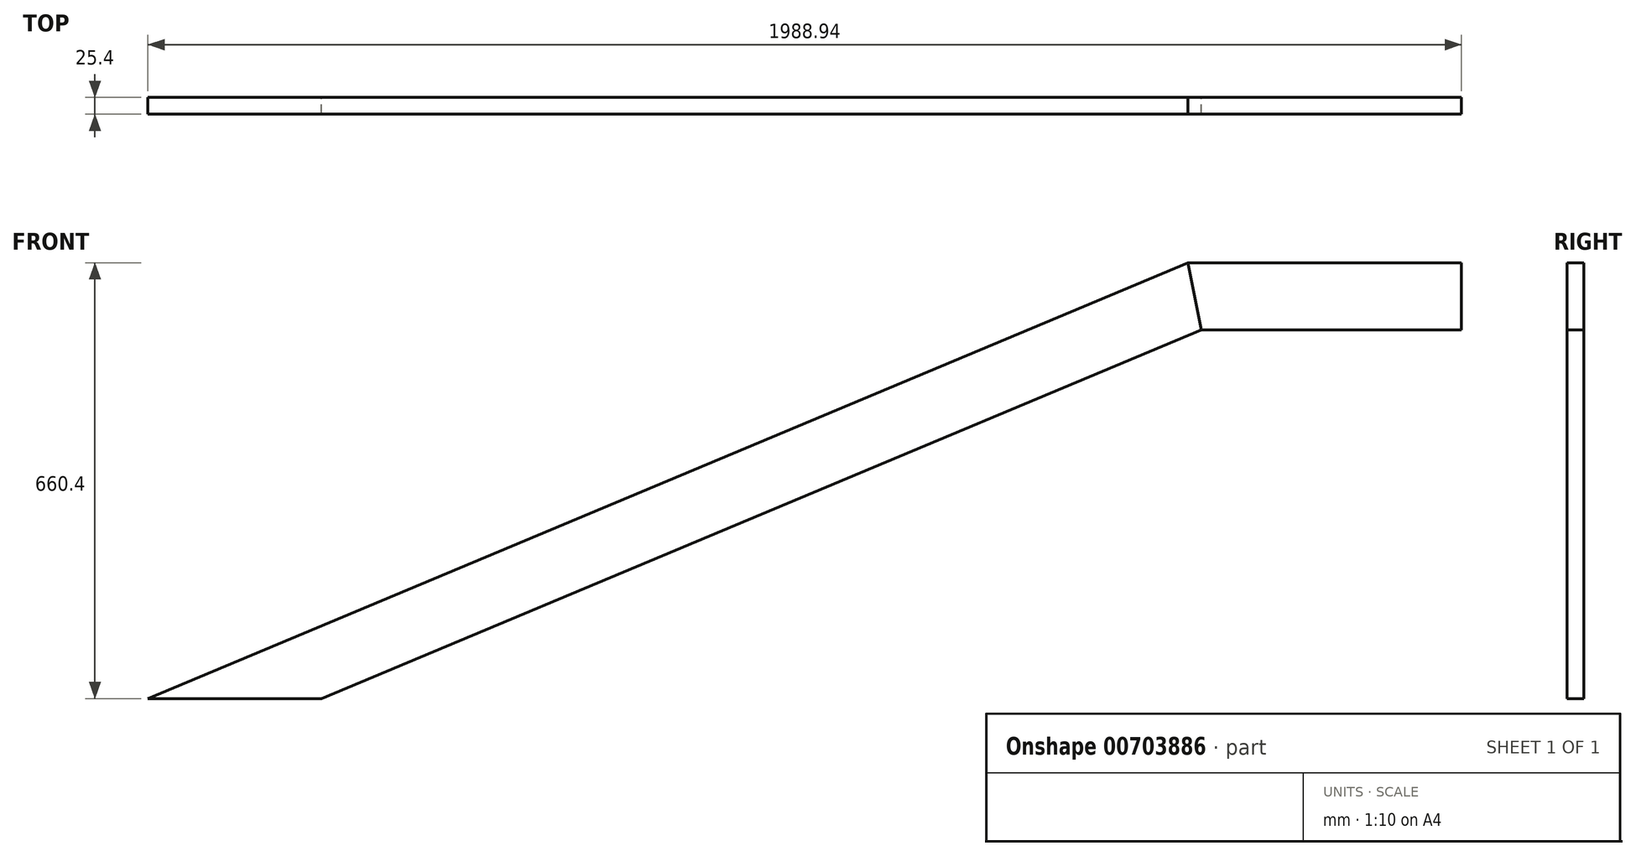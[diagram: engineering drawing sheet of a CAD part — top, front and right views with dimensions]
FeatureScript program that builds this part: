
annotation { "Feature Type Name" : "Feature", "Feature Type Description" : "" }
export const myFeature = defineFeature(function(context is Context, id is Id, definition is map)
    precondition{}
    {
        {
            var Q0;
            Q0=qCreatedBy(makeId("Front.planeOp"),FACE);
            var sketch = newSketch(context, id + "F0", { "sketchPlane" : qUnion([Q0])});
            skLineSegment(sketch, "E0", {"start": v(0, 0) * mm, "end": v(1574.8, 660.4) * mm});
            skLineSegment(sketch, "E1", {"start": v(1574.8, 660.4) * mm, "end": v(1988.94, 660.4) * mm});
            skLineSegment(sketch, "E2", {"start": v(1988.94, 660.4) * mm, "end": v(1988.94, 558.8) * mm});
            skLineSegment(sketch, "E3", {"start": v(1595.24, 558.8) * mm, "end": v(262.72, 0) * mm});
            skLineSegment(sketch, "E4", {"start": v(1988.94, 558.8) * mm, "end": v(1595.24, 558.8) * mm});
            skLineSegment(sketch, "E5", {"start": v(0, 0) * mm, "end": v(262.72, 0) * mm});
            skLineSegment(sketch, "E6", {"start": v(1574.8, 660.4) * mm, "end": v(1574.8, 0) * mm});
            skLineSegment(sketch, "E7", {"start": v(1574.8, 0) * mm, "end": v(0, 0) * mm});
            skLineSegment(sketch, "E8", {"start": v(1574.8, 660.4) * mm, "end": v(1595.24, 558.8) * mm});
            skSolve(sketch);
        }
        {
            var Q0;
            Q0=makeQuery(id+"F0.imprint","IMPRINT",FACE,{"disambiguationData":[TD([[makeQuery(id+"F0.imprint","IMPRINT",EDGE,{"derivedFrom":sQuery(id+"F0.wireOp",EDGE,"NblP0CX2-Pn9X-ETQz-nnOZ-x62gr8RrIhcG")}),1.0]])]});
            var Q1;
            Q1=makeQuery(id+"F0.imprint","IMPRINT",FACE,{"disambiguationData":[TD([[makeQuery(id+"F0.imprint","IMPRINT",EDGE,{"derivedFrom":sQuery(id+"F0.wireOp",EDGE,"E0")}),-1.0]])]});
            var Q2;
            {var subQ0=sQuery(id+"F0.wireOp",EDGE,"E8");Q2=makeQuery(id+"F0.imprint","IMPRINT",FACE,{"disambiguationData":[TD([[makeQuery(id+"F0.imprint","IMPRINT",EDGE,{"derivedFrom":subQ0}),-1.0]])]});}
            extrude(context, id + "F1", {"entities" : qUnion([Q0, Q1, Q2]), "depth" : 25.4 * mm, "offsetDistance" : 30.48 * mm});
        }
        {
            var Q0;
            {var subQ0=sQuery(id+"F0.wireOp",EDGE,"E1");Q0=makeQuery(id+"F0.imprint","IMPRINT",FACE,{"disambiguationData":[TD([[makeQuery(id+"F0.imprint","IMPRINT",EDGE,{"derivedFrom":subQ0}),-1.0]])]});}
            extrude(context, id + "F2", {"entities" : qUnion([Q0]), "depth" : 25.4 * mm, "offsetDistance" : 25.4 * mm});
        }
    });
